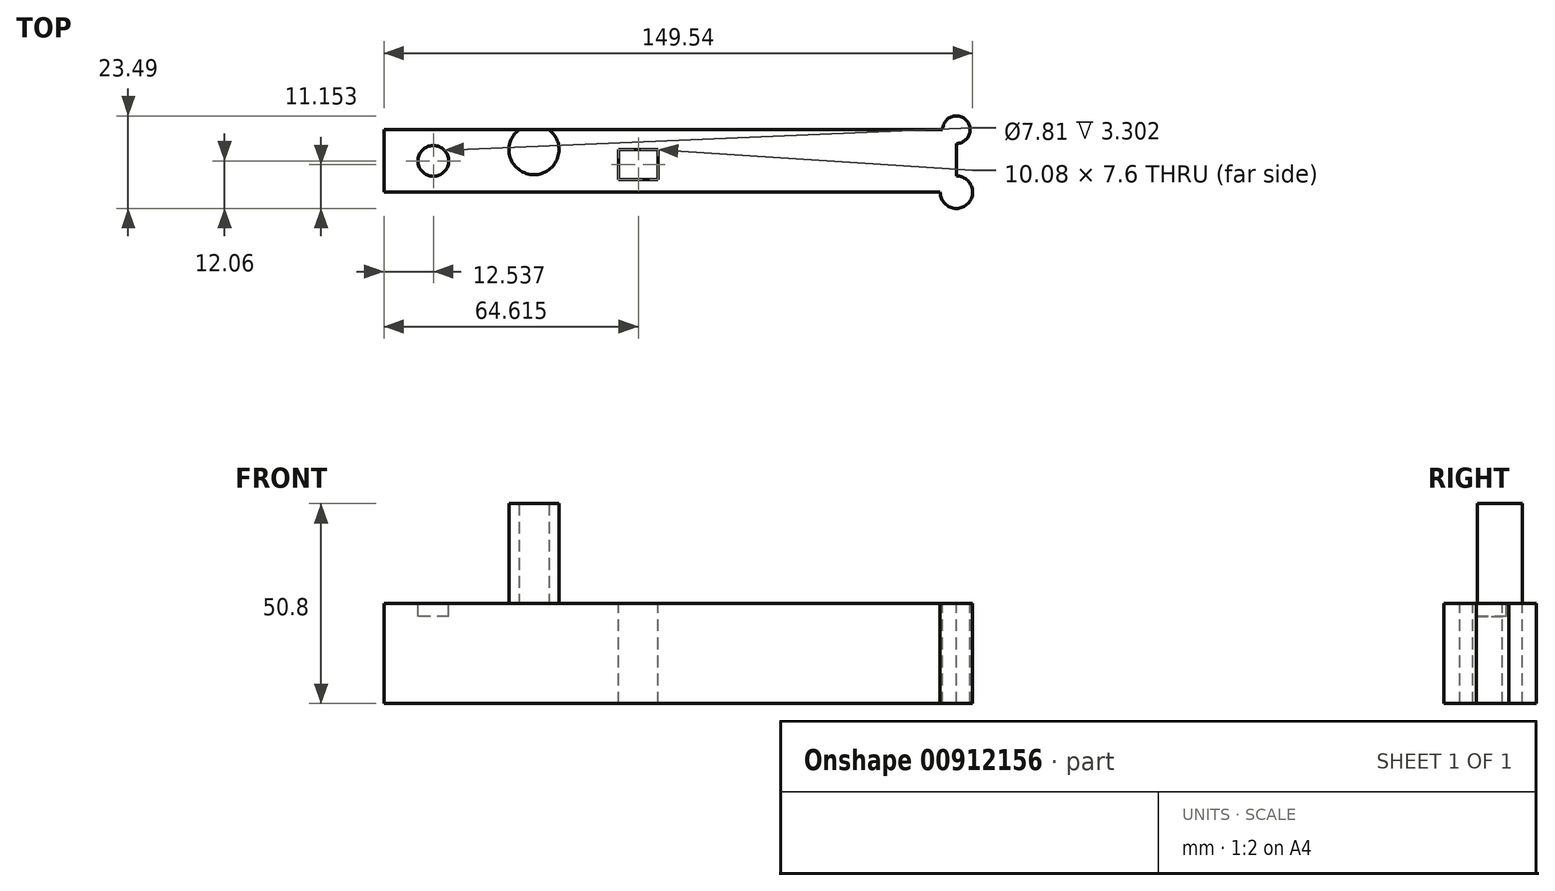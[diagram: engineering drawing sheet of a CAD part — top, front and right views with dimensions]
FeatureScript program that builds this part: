
annotation { "Feature Type Name" : "Feature", "Feature Type Description" : "" }
export const myFeature = defineFeature(function(context is Context, id is Id, definition is map)
    precondition{}
    {
        {
            var Q0;
            Q0=qCreatedBy(makeId("Top.planeOp"),FACE);
            var sketch = newSketch(context, id + "F0", { "sketchPlane" : qUnion([Q0])});
            skLineSegment(sketch, "E0.bottom", {"start": v(72.7, -7.94) * mm, "end": v(-72.7, -7.94) * mm});
            skLineSegment(sketch, "E0.top", {"start": v(72.7, 7.94) * mm, "end": v(-72.7, 7.94) * mm});
            skLineSegment(sketch, "E0.left", {"start": v(72.7, -7.94) * mm, "end": v(72.7, 7.94) * mm});
            skLineSegment(sketch, "E0.right", {"start": v(-72.7, -7.94) * mm, "end": v(-72.7, 7.94) * mm});
            skPoint(sketch, "E0.middle", {"position": v(0, 0) * mm});
            skSolve(sketch);
        }
        {
            var Q0;
            Q0=makeQuery(id+"F0.imprint","IMPRINT",FACE,{"disambiguationData":[TD([[makeQuery(id+"F0.imprint","IMPRINT",EDGE,{"derivedFrom":sQuery(id+"F0.wireOp",EDGE,"E0.bottom")}),-1.0]])]});
            extrude(context, id + "F1", {"entities" : qUnion([Q0]), "depth" : 25.4 * mm, "offsetDistance" : 25.4 * mm});
        }
        {
            var Q0;
            Q0=makeQuery(id+"F1.opExtrude","CAP_FACE",FACE,{"disambiguationData":[OSD([sQuery(id+"F0.wireOp",EDGE,"E0.bottom"),sQuery(id+"F0.wireOp",EDGE,"E0.top"),sQuery(id+"F0.wireOp",EDGE,"E0.left"),sQuery(id+"F0.wireOp",EDGE,"E0.right")])],"isStart":false});
            var sketch = newSketch(context, id + "F2", { "sketchPlane" : qUnion([Q0])});
            skCircle(sketch, "E1", {"center": v(-60.17, 0) * mm, "radius": 3.9 * mm});
            skCircle(sketch, "E2", {"center": v(-34.6, 2.86) * mm, "radius": 6.35 * mm});
            skSolve(sketch);
        }
        {
            var Q0;
            {var subQ0=sQuery(id+"F2.wireOp",EDGE,"E2");var subQ1=makeQuery(id+"F1.opExtrude","CAP_EDGE",EDGE,{"disambiguationData":[OSD([sQuery(id+"F0.wireOp",EDGE,"E0.top")])],"isStart":false});var subQ2=makeQuery(id+"F2.imprint","INTERSECT",VERTEX,{"disambiguationData":[OD(0.0)],"derivedFrom":[subQ1,subQ0]});Q0=makeQuery(id+"F2.imprint","IMPRINT",FACE,{"disambiguationData":[TD([[makeQuery(id+"F2.imprint","IMPRINT",EDGE,{"disambiguationData":[TD([[subQ2,1.0]])],"derivedFrom":subQ0}),1.0]])]});}
            extrude(context, id + "F3", {"entities" : qUnion([Q0]), "operationType" : NewBodyOperationType.ADD, "depth" : 25.4 * mm, "offsetDistance" : 25.4 * mm});
        }
        {
            var Q0;
            Q0=makeQuery(id+"F2.imprint","IMPRINT",FACE,{"disambiguationData":[TD([[makeQuery(id+"F2.imprint","IMPRINT",EDGE,{"derivedFrom":sQuery(id+"F2.wireOp",EDGE,"E1")}),1.0]])]});
            extrude(context, id + "F4", {"entities" : qUnion([Q0]), "operationType" : NewBodyOperationType.REMOVE, "oppositeDirection" : true, "depth" : 3.3 * mm, "offsetDistance" : 25.4 * mm});
        }
        {
            var Q0;
            Q0=makeQuery(id+"F2.imprint","IMPRINT",FACE,{"disambiguationData":[TD([[makeQuery(id+"F2.imprint","IMPRINT",EDGE,{"derivedFrom":sQuery(id+"F2.wireOp",EDGE,"E1")}),-1.0]])]});
            var sketch = newSketch(context, id + "F5", { "sketchPlane" : qUnion([Q0])});
            skLineSegment(sketch, "E3.bottom", {"start": v(-13.14, 2.9) * mm, "end": v(-3.05, 2.9) * mm});
            skLineSegment(sketch, "E3.top", {"start": v(-13.14, -4.7) * mm, "end": v(-3.05, -4.7) * mm});
            skLineSegment(sketch, "E3.left", {"start": v(-13.14, 2.9) * mm, "end": v(-13.14, -4.7) * mm});
            skLineSegment(sketch, "E3.right", {"start": v(-3.05, 2.9) * mm, "end": v(-3.05, -4.7) * mm});
            skSolve(sketch);
        }
        {
            var Q0;
            Q0=makeQuery(id+"F5.imprint","IMPRINT",FACE,{"disambiguationData":[TD([[makeQuery(id+"F5.imprint","IMPRINT",EDGE,{"derivedFrom":sQuery(id+"F5.wireOp",EDGE,"E3.bottom")}),-1.0]])]});
            var Q1;
            Q1=makeQuery(id+"F1.opExtrude","CAP_FACE",FACE,{"disambiguationData":[OSD([sQuery(id+"F0.wireOp",EDGE,"E0.bottom"),sQuery(id+"F0.wireOp",EDGE,"E0.top"),sQuery(id+"F0.wireOp",EDGE,"E0.left"),sQuery(id+"F0.wireOp",EDGE,"E0.right")])],"isStart":true});
            extrude(context, id + "F6", {"entities" : qUnion([Q0]), "operationType" : NewBodyOperationType.REMOVE, "endBound" : BoundingType.UP_TO_SURFACE, "oppositeDirection" : true, "depth" : 16.5 * mm, "endBoundEntityFace" : qUnion([Q1]), "offsetDistance" : 25.4 * mm});
        }
        {
            var Q0;
            Q0=makeQuery(id+"F1.opExtrude","SWEPT_FACE",FACE,{"disambiguationData":[OSD([sQuery(id+"F0.wireOp",EDGE,"E0.left")])]});
            var sketch = newSketch(context, id + "F7", { "sketchPlane" : qUnion([Q0])});
            skLineSegment(sketch, "E4.bottom", {"start": v(7.94, 25.4) * mm, "end": v(4.44, 25.4) * mm});
            skLineSegment(sketch, "E4.top", {"start": v(7.94, 0) * mm, "end": v(4.44, 0) * mm});
            skLineSegment(sketch, "E4.left", {"start": v(7.94, 25.4) * mm, "end": v(7.94, 0) * mm});
            skLineSegment(sketch, "E4.right", {"start": v(4.44, 25.4) * mm, "end": v(4.44, 0) * mm});
            skSolve(sketch);
        }
        {
            var Q0;
            Q0=makeQuery(id+"F7.imprint","IMPRINT",FACE,{"disambiguationData":[TD([[makeQuery(id+"F7.imprint","IMPRINT",EDGE,{"derivedFrom":sQuery(id+"F7.wireOp",EDGE,"E4.bottom")}),-1.0]])]});
            var Q1;
            Q1=sQuery(id+"F7.wireOp",EDGE,"E4.left");
            revolve(context, id + "F8", {"operationType" : NewBodyOperationType.ADD, "surfaceOperationType" : NewSurfaceOperationType.NEW, "entities" : qUnion([Q0]), "axis" : qUnion([Q1]), "revolveType" : RevolveType.FULL});
        }
        {
            var Q0;
            Q0=makeQuery(id+"F2.imprint","IMPRINT",FACE,{"disambiguationData":[TD([[makeQuery(id+"F2.imprint","IMPRINT",EDGE,{"derivedFrom":sQuery(id+"F2.wireOp",EDGE,"E1")}),-1.0]])]});
            var sketch = newSketch(context, id + "F9", { "sketchPlane" : qUnion([Q0])});
            skCircle(sketch, "E5", {"center": v(72.7, -7.94) * mm, "radius": 4.12 * mm});
            skSolve(sketch);
        }
        {
            var Q0;
            Q0 = qSketchRegion(id + "F9", true);
            var Q1;
            Q1=makeQuery(id+"F8.boolean.opBoolean","MERGE",FACE,{"derivedFrom":[makeQuery(id+"F1.opExtrude","CAP_FACE",FACE,{"disambiguationData":[OSD([sQuery(id+"F0.wireOp",EDGE,"E0.bottom"),sQuery(id+"F0.wireOp",EDGE,"E0.top"),sQuery(id+"F0.wireOp",EDGE,"E0.left"),sQuery(id+"F0.wireOp",EDGE,"E0.right")])],"isStart":true}),makeQuery(id+"F8.opRevolve","SWEPT_FACE",FACE,{"disambiguationData":[OSD([sQuery(id+"F7.wireOp",EDGE,"E4.top")])]})]});
            extrude(context, id + "F10", {"entities" : qUnion([Q0]), "operationType" : NewBodyOperationType.ADD, "endBound" : BoundingType.UP_TO_SURFACE, "oppositeDirection" : true, "depth" : 25.4 * mm, "endBoundEntityFace" : qUnion([Q1]), "offsetDistance" : 25.4 * mm});
        }
    });
